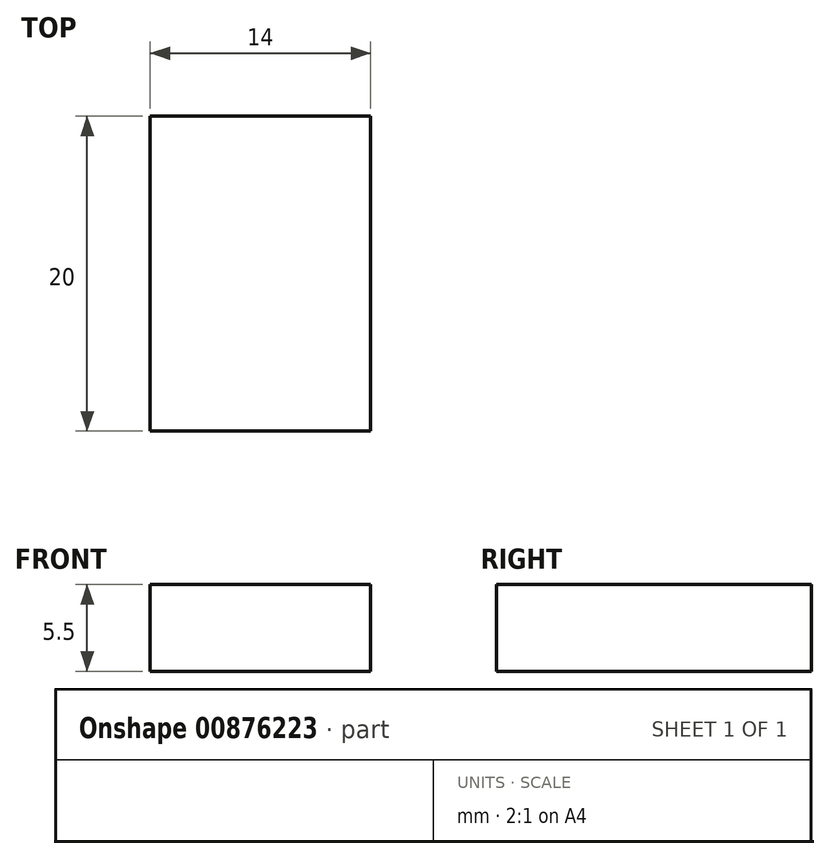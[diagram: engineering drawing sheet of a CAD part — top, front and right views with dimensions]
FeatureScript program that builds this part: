
annotation { "Feature Type Name" : "Feature", "Feature Type Description" : "" }
export const myFeature = defineFeature(function(context is Context, id is Id, definition is map)
    precondition{}
    {
        {
            var Q0;
            Q0=qCreatedBy(makeId("Top.planeOp"),FACE);
            var sketch = newSketch(context, id + "F0", { "sketchPlane" : qUnion([Q0])});
            skLineSegment(sketch, "E0.bottom", {"start": v(-7, 10) * mm, "end": v(7, 10) * mm});
            skLineSegment(sketch, "E0.top", {"start": v(-7, -10) * mm, "end": v(7, -10) * mm});
            skLineSegment(sketch, "E0.left", {"start": v(-7, 10) * mm, "end": v(-7, -10) * mm});
            skLineSegment(sketch, "E0.right", {"start": v(7, 10) * mm, "end": v(7, -10) * mm});
            skPoint(sketch, "E0.middle", {"position": v(0, 0) * mm});
            skSolve(sketch);
        }
        {
            var Q0;
            Q0=makeQuery(id+"F0.imprint","IMPRINT",FACE,{"disambiguationData":[TD([[makeQuery(id+"F0.imprint","IMPRINT",EDGE,{"derivedFrom":sQuery(id+"F0.wireOp",EDGE,"E0.bottom")}),-1.0]])]});
            extrude(context, id + "F1", {"entities" : qUnion([Q0]), "depth" : 5.5 * mm});
        }
    });
